# Revit family: FU_Inspec_Campus_1-5
name_source: partatom
category: Furniture
units: mm (PartAtom-declared; Revit-internal decimal feet)

## family parameters
Always vertical = Yes
Cut with Voids When Loaded = No
OmniClass Number = 23.40.20.00
OmniClass Title = General Furniture and Specialties
Room Calculation Point = No
Shared = No
Work Plane-Based = No

## types (3) — shared parameters
Assembly Code = E2020
Keynote = 46.B
Manufacturer = Inspec
URL = https://inspecfurniture.com
zero-valued in all types: Default Elevation

## per-type parameters (varying)
| type | Back Material | Description | Frame Material | Model | Seat Material |
| Campus 1.4 | Laminate - Compact - White | Chair with seat and back in ash or oak on a powder coated or chromium plated sled base. | Metal - Chrome - Polished | campus 1.4 | Laminate - Compact - White |
| Campus 1.5 | Wood - Veneer - Oak | Chair with upholstered seat and back in ash or oak on a powder coated or chromium plated sled base. | Laminate - Compact - Black | campus 1.5 | Fabric - Red |
| Campus 1.6 | Fabric - Red | Fully upholstered chair on a powder coated or chromium plated steel sled base. | Laminate - Compact - White | campus 1.6 | Fabric - Red |

## geometry (parser evidence)
native form markers: Blend x6, Sweep x2
no freeform markers — native parametric forms only
